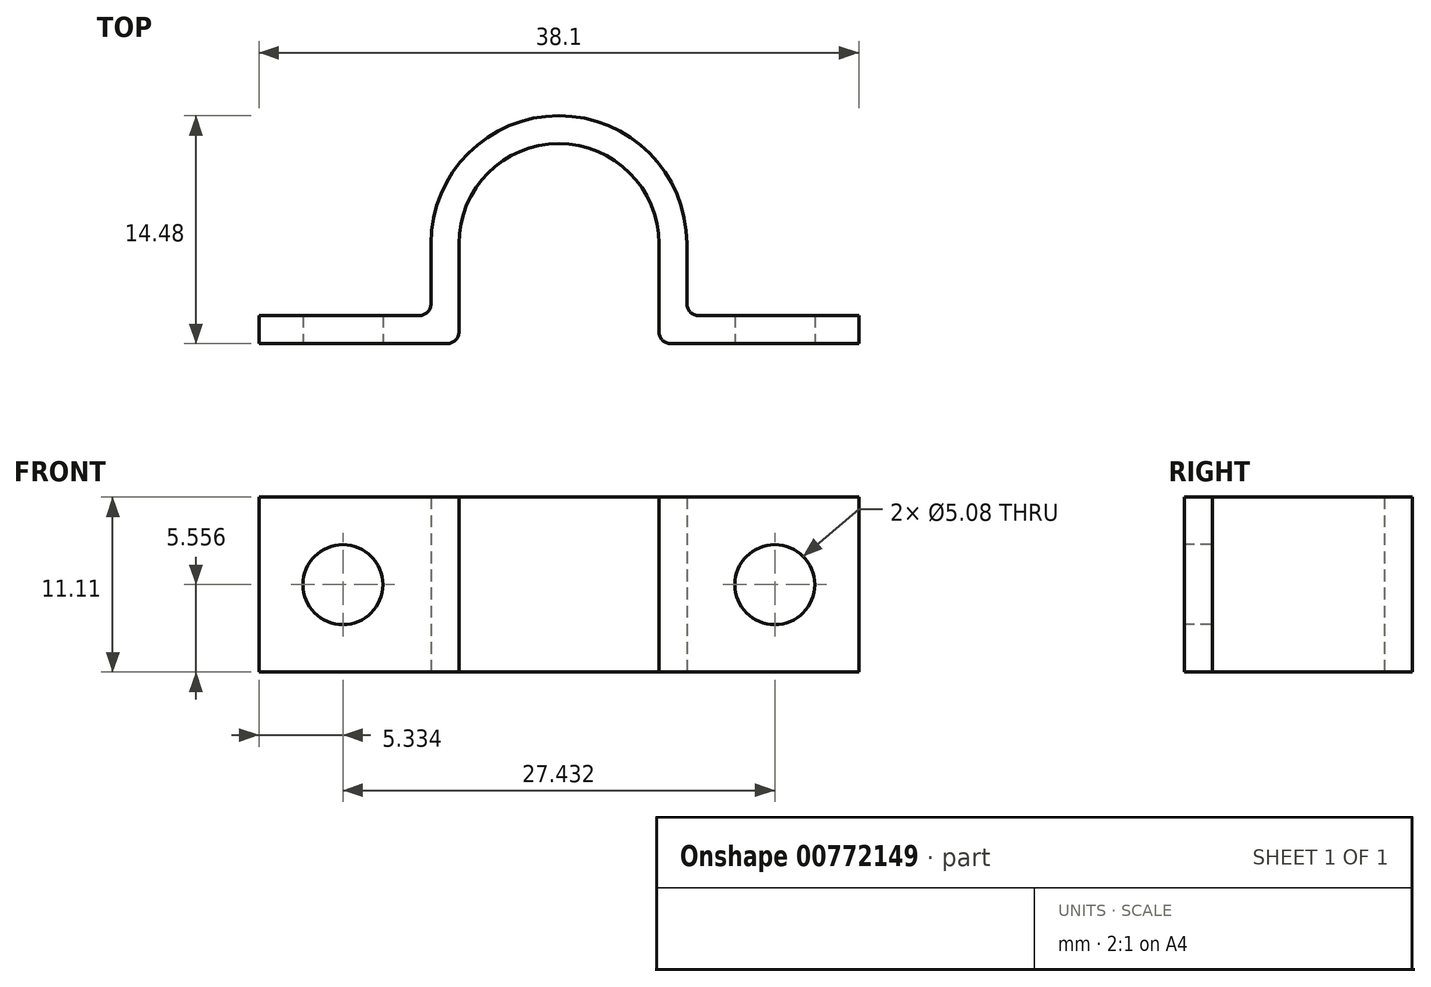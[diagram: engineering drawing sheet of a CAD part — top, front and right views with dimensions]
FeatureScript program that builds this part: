
annotation { "Feature Type Name" : "Feature", "Feature Type Description" : "" }
export const myFeature = defineFeature(function(context is Context, id is Id, definition is map)
    precondition{}
    {
        {
            var Q0;
            Q0=qCreatedBy(makeId("Top.planeOp"),FACE);
            var sketch = newSketch(context, id + "F0", { "sketchPlane" : qUnion([Q0])});
            skArc(sketch, "E0", {"start": v(-6.35, 0) * mm, "mid": v(0, 6.35) * mm, "end": v(6.35, 0) * mm});
            skLineSegment(sketch, "E1", {"start": v(-6.35, 0) * mm, "end": v(-6.35, -6.35) * mm});
            skLineSegment(sketch, "E2", {"start": v(6.35, 0) * mm, "end": v(6.35, -6.35) * mm});
            skLineSegment(sketch, "E3", {"start": v(6.35, -6.35) * mm, "end": v(19.05, -6.35) * mm});
            skLineSegment(sketch, "E4", {"start": v(-6.35, -6.35) * mm, "end": v(-19.05, -6.35) * mm});
            skLineSegment(sketch, "E5.0", {"start": v(-8.13, -4.57) * mm, "end": v(-19.05, -4.57) * mm});
            skLineSegment(sketch, "E5.1", {"start": v(8.13, -4.57) * mm, "end": v(19.05, -4.57) * mm});
            skLineSegment(sketch, "E5.2", {"start": v(8.13, 0) * mm, "end": v(8.13, -4.57) * mm});
            skArc(sketch, "E5.3", {"start": v(-8.13, 0) * mm, "mid": v(0, 8.13) * mm, "end": v(8.13, 0) * mm});
            skLineSegment(sketch, "E5.4", {"start": v(-8.13, 0) * mm, "end": v(-8.13, -4.57) * mm});
            skLineSegment(sketch, "E6", {"start": v(-19.05, -4.57) * mm, "end": v(-19.05, -6.35) * mm});
            skLineSegment(sketch, "E7", {"start": v(19.05, -4.57) * mm, "end": v(19.05, -6.35) * mm});
            skSolve(sketch);
        }
        {
            var Q0;
            Q0 = qSketchRegion(id + "F0", true);
            extrude(context, id + "F1", {"entities" : qUnion([Q0]), "depth" : 11.1 * mm, "offsetDistance" : 25.4 * mm});
        }
        {
            var Q0;
            Q0=makeQuery(id+"F1.opExtrude","SWEPT_EDGE",EDGE,{"disambiguationData":[OSD([sQuery(id+"F0.wireOp",EDGE,"E1"),sQuery(id+"F0.wireOp",EDGE,"E4")])]});
            var Q1;
            Q1=makeQuery(id+"F1.opExtrude","SWEPT_EDGE",EDGE,{"disambiguationData":[OSD([sQuery(id+"F0.wireOp",EDGE,"E2"),sQuery(id+"F0.wireOp",EDGE,"E3")])]});
            var Q2;
            Q2=makeQuery(id+"F1.opExtrude","SWEPT_EDGE",EDGE,{"disambiguationData":[OSD([sQuery(id+"F0.wireOp",EDGE,"E5.1"),sQuery(id+"F0.wireOp",EDGE,"E5.2")])]});
            var Q3;
            Q3=makeQuery(id+"F1.opExtrude","SWEPT_EDGE",EDGE,{"disambiguationData":[OSD([sQuery(id+"F0.wireOp",EDGE,"E5.0"),sQuery(id+"F0.wireOp",EDGE,"E5.4")])]});
            fillet(context, id + "F2", {"entities" : qUnion([Q0, Q1, Q2, Q3]), "radius" : 0.76 * mm, "tangentPropagation" : true, "allowEdgeOverflow" : false});
        }
        {
            var Q0;
            Q0=makeQuery(id+"F1.opExtrude","SWEPT_FACE",FACE,{"disambiguationData":[OSD([sQuery(id+"F0.wireOp",EDGE,"E4")])]});
            var sketch = newSketch(context, id + "F3", { "sketchPlane" : qUnion([Q0])});
            skCircle(sketch, "E8", {"center": v(-13.72, 5.56) * mm, "radius": 2.54 * mm});
            skCircle(sketch, "E9", {"center": v(13.72, 5.56) * mm, "radius": 2.54 * mm});
            skSolve(sketch);
        }
        {
            var Q0;
            Q0 = qSketchRegion(id + "F3", true);
            extrude(context, id + "F4", {"entities" : qUnion([Q0]), "operationType" : NewBodyOperationType.REMOVE, "endBound" : BoundingType.THROUGH_ALL, "oppositeDirection" : true, "depth" : 25.4 * mm, "offsetDistance" : 25.4 * mm});
        }
    });
